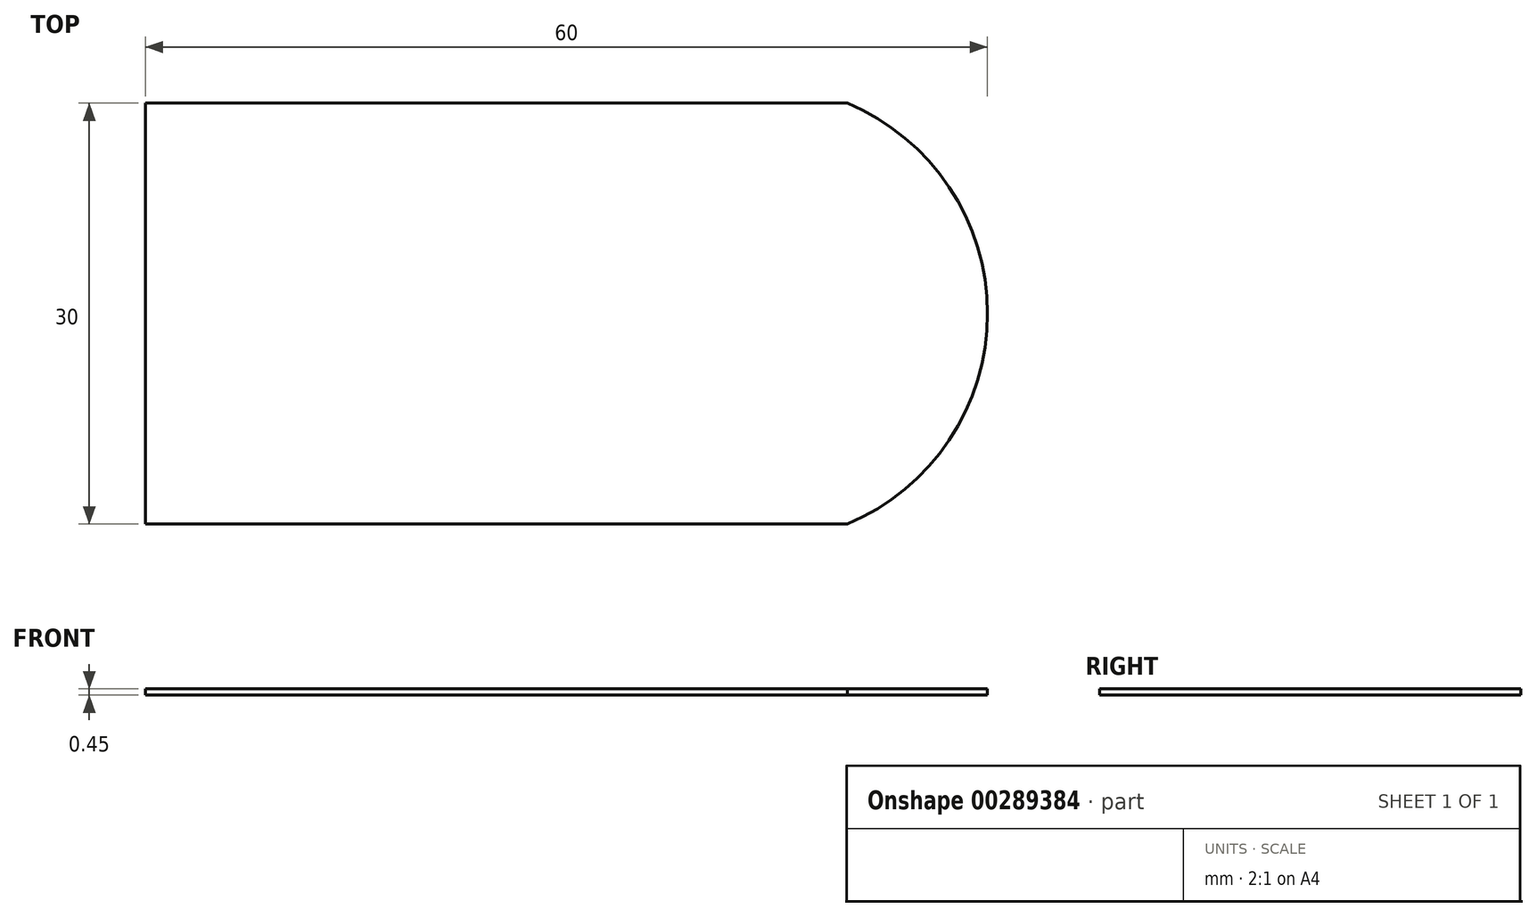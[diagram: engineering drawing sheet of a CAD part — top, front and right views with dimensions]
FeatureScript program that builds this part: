
annotation { "Feature Type Name" : "Feature", "Feature Type Description" : "" }
export const myFeature = defineFeature(function(context is Context, id is Id, definition is map)
    precondition{}
    {
        {
            var Q0;
            Q0=qCreatedBy(makeId("Top.planeOp"),FACE);
            var sketch = newSketch(context, id + "F0", { "sketchPlane" : qUnion([Q0])});
            skLineSegment(sketch, "E0", {"start": v(0, 0) * mm, "end": v(0, 30) * mm});
            skLineSegment(sketch, "E1", {"start": v(0, 30) * mm, "end": v(50, 30) * mm});
            skLineSegment(sketch, "E2", {"start": v(50, 30) * mm, "end": v(50, 0) * mm});
            skLineSegment(sketch, "E3", {"start": v(50, 0) * mm, "end": v(0, 0) * mm});
            skArc(sketch, "E4", {"start": v(50, 0) * mm, "mid": v(60, 15) * mm, "end": v(50, 30) * mm});
            skLineSegment(sketch, "E5", {"start": v(-31.14, -6.14) * mm, "end": v(-1.14, -6.14) * mm});
            skLineSegment(sketch, "E6", {"start": v(-1.14, -6.14) * mm, "end": v(-1.14, -56.14) * mm});
            skLineSegment(sketch, "E7", {"start": v(-1.14, -56.14) * mm, "end": v(-31.14, -56.14) * mm});
            skLineSegment(sketch, "E8", {"start": v(-31.14, -56.14) * mm, "end": v(-31.14, -6.14) * mm});
            skArc(sketch, "E9", {"start": v(-31.14, -56.14) * mm, "mid": v(-16.14, -66.14) * mm, "end": v(-1.14, -56.14) * mm});
            skSolve(sketch);
        }
        {
            var Q0;
            Q0=makeQuery(id+"F0.imprint","IMPRINT",FACE,{"disambiguationData":[TD([[makeQuery(id+"F0.imprint","IMPRINT",EDGE,{"derivedFrom":sQuery(id+"F0.wireOp",EDGE,"E0")}),-1.0]])]});
            var Q1;
            Q1=makeQuery(id+"F0.imprint","IMPRINT",FACE,{"disambiguationData":[TD([[makeQuery(id+"F0.imprint","IMPRINT",EDGE,{"derivedFrom":sQuery(id+"F0.wireOp",EDGE,"E2")}),1.0]])]});
            extrude(context, id + "F1", {"entities" : qUnion([Q0, Q1]), "depth" : .45 * mm});
        }
        {
            var Q0;
            Q0=makeQuery(id+"F1.opExtrude","SWEPT_BODY",BODY,{"disambiguationData":[OSD([sQuery(id+"F0.wireOp",EDGE,"E0"),sQuery(id+"F0.wireOp",EDGE,"E1"),sQuery(id+"F0.wireOp",EDGE,"E3"),sQuery(id+"F0.wireOp",EDGE,"E4")])]});
            transform(context, id + "F2", {"entities" : qUnion([Q0]), "transformType" : TransformType.TRANSLATION_3D, "dx" : 0 * mm, "dy" : 0 * mm, "dz" : 0 * mm, "makeCopy" : true});
        }
        {
            var Q0;
            Q0=makeQuery(id+"F2.opPattern","COPY",BODY,{"derivedFrom":makeQuery(id+"F1.opExtrude","SWEPT_BODY",BODY,{"disambiguationData":[OSD([sQuery(id+"F0.wireOp",EDGE,"E0"),sQuery(id+"F0.wireOp",EDGE,"E1"),sQuery(id+"F0.wireOp",EDGE,"E3"),sQuery(id+"F0.wireOp",EDGE,"E4")])]}),"instanceName":"1"});
            deleteBodies(context, id + "F3", {"entities" : qUnion([Q0])});
        }
    });
